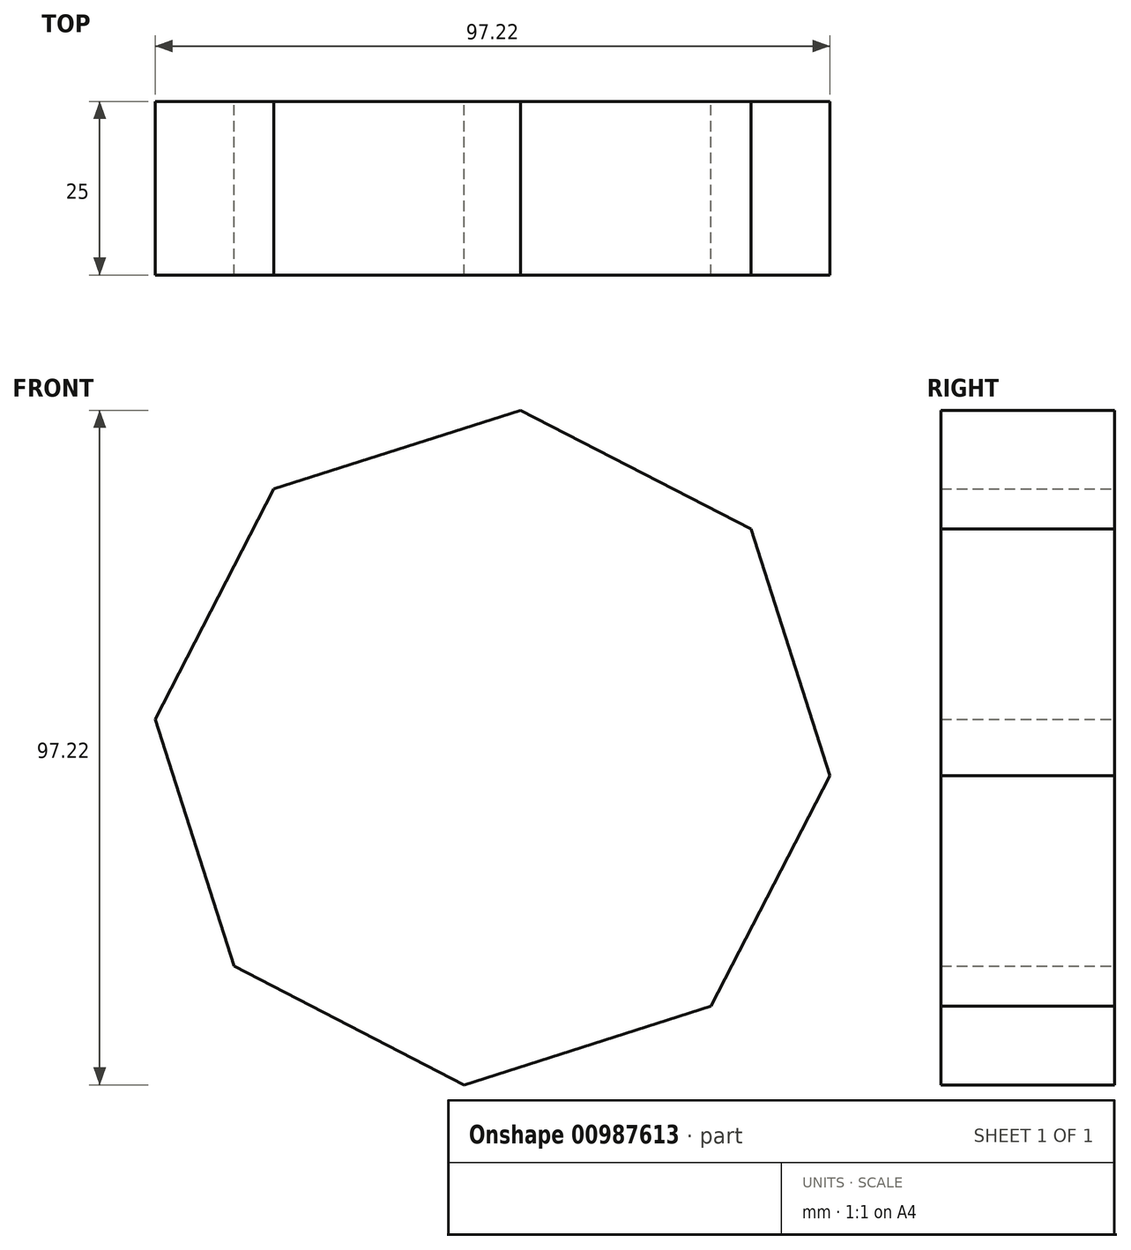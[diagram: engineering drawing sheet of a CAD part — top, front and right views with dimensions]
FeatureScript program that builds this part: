
annotation { "Feature Type Name" : "Feature", "Feature Type Description" : "" }
export const myFeature = defineFeature(function(context is Context, id is Id, definition is map)
    precondition{}
    {
        {
            var Q0;
            Q0=qCreatedBy(makeId("Front.planeOp"),FACE);
            var sketch = newSketch(context, id + "F0", { "sketchPlane" : qUnion([Q0])});
            skCircle(sketch, "E0.cCircle", {"center": v(0, 0) * mm, "radius": 45.07 * mm, "construction": true});
            skLineSegment(sketch, "E0.0", {"start": v(-48.61, 4.07) * mm, "end": v(-31.5, 37.25) * mm});
            skLineSegment(sketch, "E0.1", {"start": v(-31.5, 37.25) * mm, "end": v(4.07, 48.61) * mm});
            skLineSegment(sketch, "E0.2", {"start": v(4.07, 48.61) * mm, "end": v(37.25, 31.5) * mm});
            skLineSegment(sketch, "E0.3", {"start": v(37.25, 31.5) * mm, "end": v(48.61, -4.07) * mm});
            skLineSegment(sketch, "E0.4", {"start": v(48.61, -4.07) * mm, "end": v(31.5, -37.25) * mm});
            skLineSegment(sketch, "E0.5", {"start": v(31.5, -37.25) * mm, "end": v(-4.07, -48.61) * mm});
            skLineSegment(sketch, "E0.6", {"start": v(-4.07, -48.61) * mm, "end": v(-37.25, -31.5) * mm});
            skLineSegment(sketch, "E0.7", {"start": v(-37.25, -31.5) * mm, "end": v(-48.61, 4.07) * mm});
            skPoint(sketch, "E0.0.midPoint", {"position": v(-40.05, 20.66) * mm});
            skSolve(sketch);
        }
        {
            var Q0;
            Q0 = qSketchRegion(id + "F0", true);
            extrude(context, id + "F1", {"entities" : qUnion([Q0]), "depth" : 25 * mm, "offsetDistance" : 25 * mm});
        }
    });
